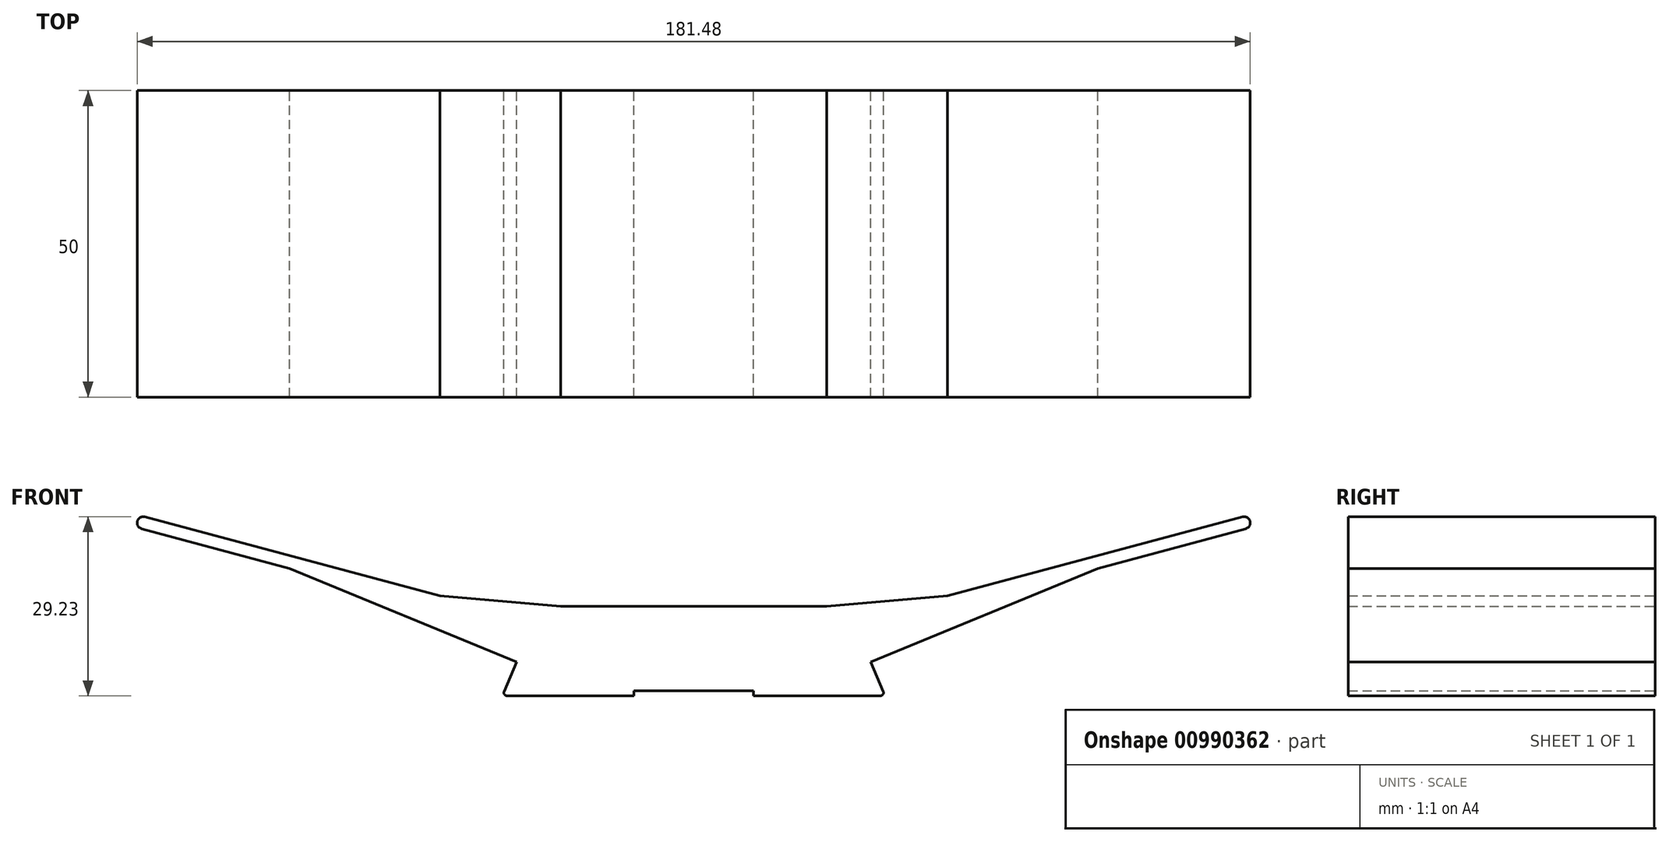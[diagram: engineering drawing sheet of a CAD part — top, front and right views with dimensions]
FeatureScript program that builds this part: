
annotation { "Feature Type Name" : "Feature", "Feature Type Description" : "" }
export const myFeature = defineFeature(function(context is Context, id is Id, definition is map)
    precondition{}
    {
        {
            var Q0;
            Q0=qCreatedBy(makeId("Front.planeOp"),FACE);
            var sketch = newSketch(context, id + "F0", { "sketchPlane" : qUnion([Q0])});
            skLineSegment(sketch, "E0", {"start": v(26.7, -11.58) * mm, "end": v(28.75, -6.78) * mm});
            skArc(sketch, "E1.filletArc", {"start": v(26.7, -11.58) * mm, "mid": v(26.74, -12.05) * mm, "end": v(27.15, -12.28) * mm});
            skLineSegment(sketch, "E2", {"start": v(27.15, -12.28) * mm, "end": v(47.85, -12.28) * mm});
            skLineSegment(sketch, "E3", {"start": v(47.85, -12.28) * mm, "end": v(47.85, -11.48) * mm});
            skLineSegment(sketch, "E4", {"start": v(28.75, -6.78) * mm, "end": v(35.82, 0.3) * mm});
            skLineSegment(sketch, "E5", {"start": v(35.82, 0.3) * mm, "end": v(15.9, 2.04) * mm});
            skLineSegment(sketch, "E6", {"start": v(15.9, 2.04) * mm, "end": v(-32.4, 14.98) * mm});
            skLineSegment(sketch, "E7.0", {"start": v(16.24, 4.02) * mm, "end": v(-31.89, 16.91) * mm});
            skLineSegment(sketch, "E7.4", {"start": v(35.9, 2.3) * mm, "end": v(16.24, 4.02) * mm});
            skArc(sketch, "E8", {"start": v(-31.89, 16.91) * mm, "mid": v(-33.1, 16.2) * mm, "end": v(-32.4, 14.98) * mm});
            skLineSegment(sketch, "E9", {"start": v(47.85, -11.48) * mm, "end": v(57.6, -11.48) * mm});
            skLineSegment(sketch, "E10", {"start": v(35.9, 2.3) * mm, "end": v(57.6, 2.3) * mm});
            skLineSegment(sketch, "E11", {"start": v(28.75, -6.78) * mm, "end": v(-8.25, 8.5) * mm});
            skLineSegment(sketch, "E12", {"start": v(57.6, 2.3) * mm, "end": v(57.6, -11.48) * mm});
            skSolve(sketch);
        }
        {
            var Q0;
            Q0=makeQuery(id+"F0.imprint","IMPRINT",FACE,{"disambiguationData":[TD([[makeQuery(id+"F0.imprint","IMPRINT",EDGE,{"derivedFrom":sQuery(id+"F0.wireOp",EDGE,"E0")}),-1.0]])]});
            var Q1;
            Q1=makeQuery(id+"F0.imprint","IMPRINT",FACE,{"disambiguationData":[TD([[makeQuery(id+"F0.imprint","IMPRINT",EDGE,{"derivedFrom":sQuery(id+"F0.wireOp",EDGE,"E4")}),1.0]])]});
            extrude(context, id + "F1", {"entities" : qUnion([Q0, Q1]), "depth" : 50 * mm, "offsetDistance" : 25 * mm});
        }
        {
            var Q0;
            Q0=makeQuery(id+"F1.opExtrude","SWEPT_BODY",BODY,{"disambiguationData":[OSD([sQuery(id+"F0.wireOp",EDGE,"E0"),sQuery(id+"F0.wireOp",EDGE,"E1.filletArc"),sQuery(id+"F0.wireOp",EDGE,"E2"),sQuery(id+"F0.wireOp",EDGE,"E3"),sQuery(id+"F0.wireOp",EDGE,"E6"),sQuery(id+"F0.wireOp",EDGE,"E7.0"),sQuery(id+"F0.wireOp",EDGE,"E7.4"),sQuery(id+"F0.wireOp",EDGE,"E8"),sQuery(id+"F0.wireOp",EDGE,"E9"),sQuery(id+"F0.wireOp",EDGE,"E10"),sQuery(id+"F0.wireOp",EDGE,"E11"),sQuery(id+"F0.wireOp",EDGE,"E12")])]});
            var Q1;
            Q1=makeQuery(id+"F1.opExtrude","SWEPT_FACE",FACE,{"disambiguationData":[OSD([sQuery(id+"F0.wireOp",EDGE,"E12")])]});
            mirror(context, id + "F2", {"operationType" : NewBodyOperationType.ADD, "entities" : qUnion([Q0]), "mirrorPlane" : qUnion([Q1])});
        }
    });
